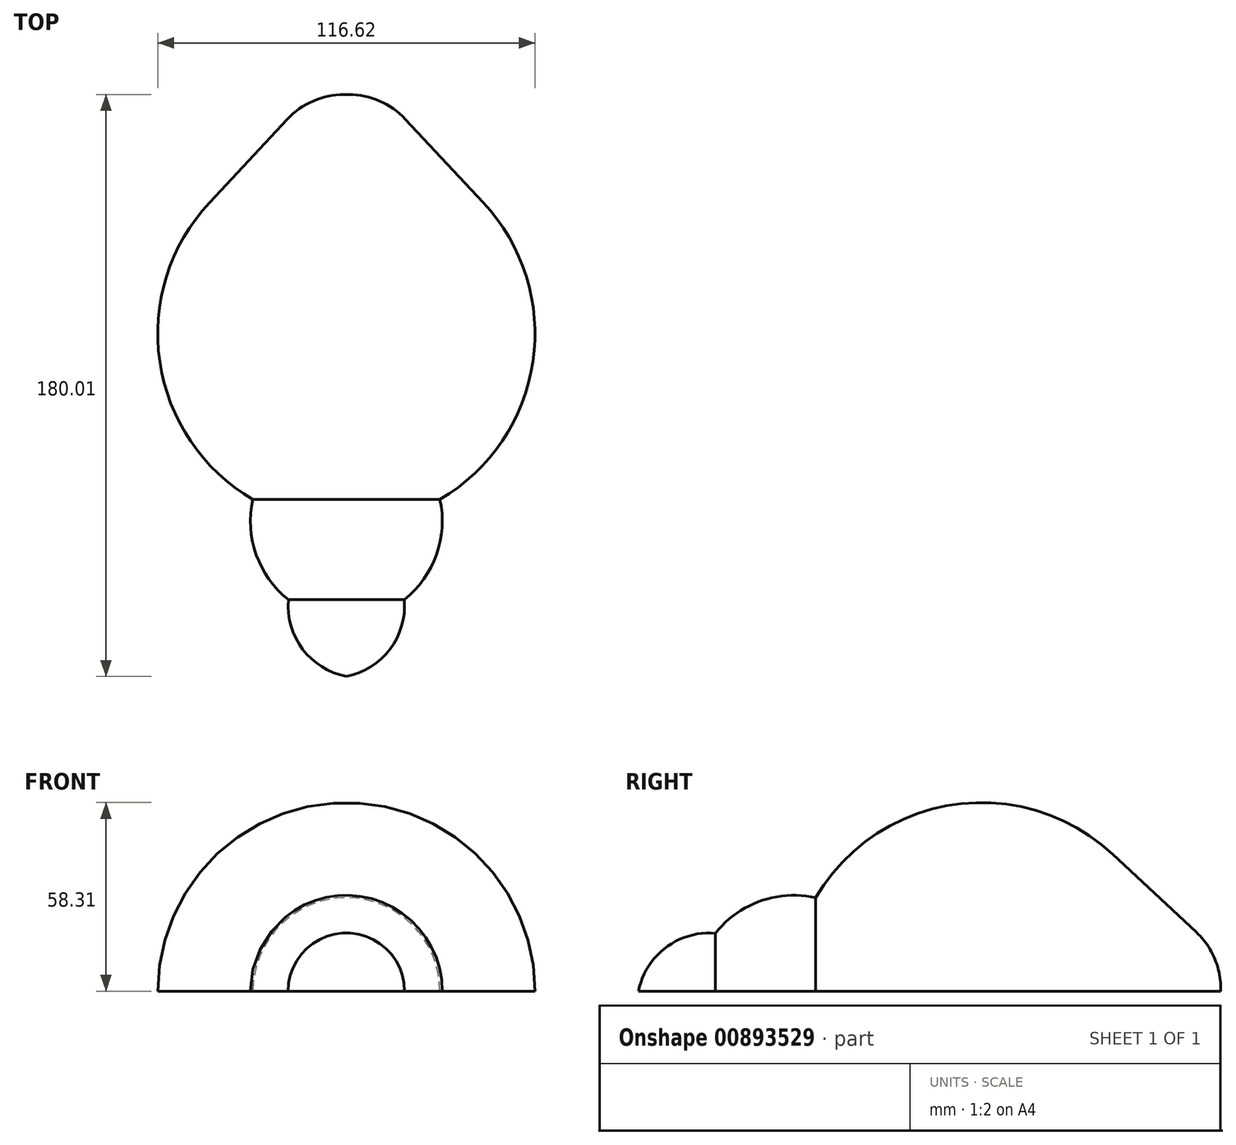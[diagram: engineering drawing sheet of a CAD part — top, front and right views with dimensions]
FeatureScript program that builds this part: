
annotation { "Feature Type Name" : "Feature", "Feature Type Description" : "" }
export const myFeature = defineFeature(function(context is Context, id is Id, definition is map)
    precondition{}
    {
        {
            var Q0;
            Q0=qCreatedBy(makeId("Top.planeOp"),FACE);
            var sketch = newSketch(context, id + "F0", { "sketchPlane" : qUnion([Q0])});
            skArc(sketch, "E0", {"start": v(17.9, -30.96) * mm, "mid": v(27.87, -17.07) * mm, "end": v(28.9, 0) * mm});
            skArc(sketch, "E1", {"start": v(0, -54.77) * mm, "mid": v(13.5, -46.29) * mm, "end": v(17.9, -30.96) * mm});
            skArc(sketch, "E2", {"start": v(28.9, 0) * mm, "mid": v(57.69, 42.7) * mm, "end": v(42.32, 91.86) * mm});
            skLineSegment(sketch, "E3", {"start": v(42.32, 91.86) * mm, "end": v(18.24, 117.66) * mm});
            skArc(sketch, "E4", {"start": v(18.24, 117.66) * mm, "mid": v(9.94, 123.42) * mm, "end": v(0, 125.23) * mm});
            skLineSegment(sketch, "E5", {"start": v(0, 125.23) * mm, "end": v(0, -54.77) * mm});
            skLineSegment(sketch, "E6", {"start": v(17.9, -30.96) * mm, "end": v(0, -30.96) * mm, "construction": true});
            skLineSegment(sketch, "E7", {"start": v(28.9, 0) * mm, "end": v(0, 0) * mm, "construction": true});
            skLineSegment(sketch, "E8", {"start": v(42.32, 91.86) * mm, "end": v(0, 91.86) * mm, "construction": true});
            skSolve(sketch);
        }
        {
            var Q0;
            Q0=makeQuery(id+"F0.imprint","IMPRINT",FACE,{"disambiguationData":[TD([[makeQuery(id+"F0.imprint","IMPRINT",EDGE,{"derivedFrom":sQuery(id+"F0.wireOp",EDGE,"E0")}),1.0]])]});
            var Q1;
            Q1=sQuery(id+"F0.wireOp",EDGE,"E5");
            revolve(context, id + "F1", {"surfaceOperationType" : NewSurfaceOperationType.NEW, "entities" : qUnion([Q0]), "axis" : qUnion([Q1]), "revolveType" : RevolveType.FULL});
        }
        {
            var Q0;
            Q0=qCreatedBy(makeId("Front.planeOp"),FACE);
            var sketch = newSketch(context, id + "F2", { "sketchPlane" : qUnion([Q0])});
            skLineSegment(sketch, "E9.bottom", {"start": v(0, 0) * mm, "end": v(63.94, 0) * mm});
            skLineSegment(sketch, "E9.top", {"start": v(0, -64.42) * mm, "end": v(63.94, -64.42) * mm});
            skLineSegment(sketch, "E9.left", {"start": v(0, 0) * mm, "end": v(0, -64.42) * mm});
            skLineSegment(sketch, "E9.right", {"start": v(63.94, 0) * mm, "end": v(63.94, -64.42) * mm});
            skLineSegment(sketch, "E10.bottom", {"start": v(0, 0) * mm, "end": v(-67.02, 0) * mm});
            skLineSegment(sketch, "E10.top", {"start": v(0, -64.42) * mm, "end": v(-67.02, -64.42) * mm});
            skLineSegment(sketch, "E10.right", {"start": v(-67.02, 0) * mm, "end": v(-67.02, -64.42) * mm});
            skSolve(sketch);
        }
        {
            var Q0;
            Q0 = qSketchRegion(id + "F2", true);
            extrude(context, id + "F3", {"entities" : qUnion([Q0]), "operationType" : NewBodyOperationType.REMOVE, "endBound" : BoundingType.THROUGH_ALL, "oppositeDirection" : true, "depth" : 25 * mm, "offsetDistance" : 25 * mm, "hasSecondDirection" : true, "secondDirectionBound" : SecondDirectionBoundingType.THROUGH_ALL, "secondDirectionOppositeDirection" : false, "secondDirectionDepth" : 25 * mm});
        }
    });
